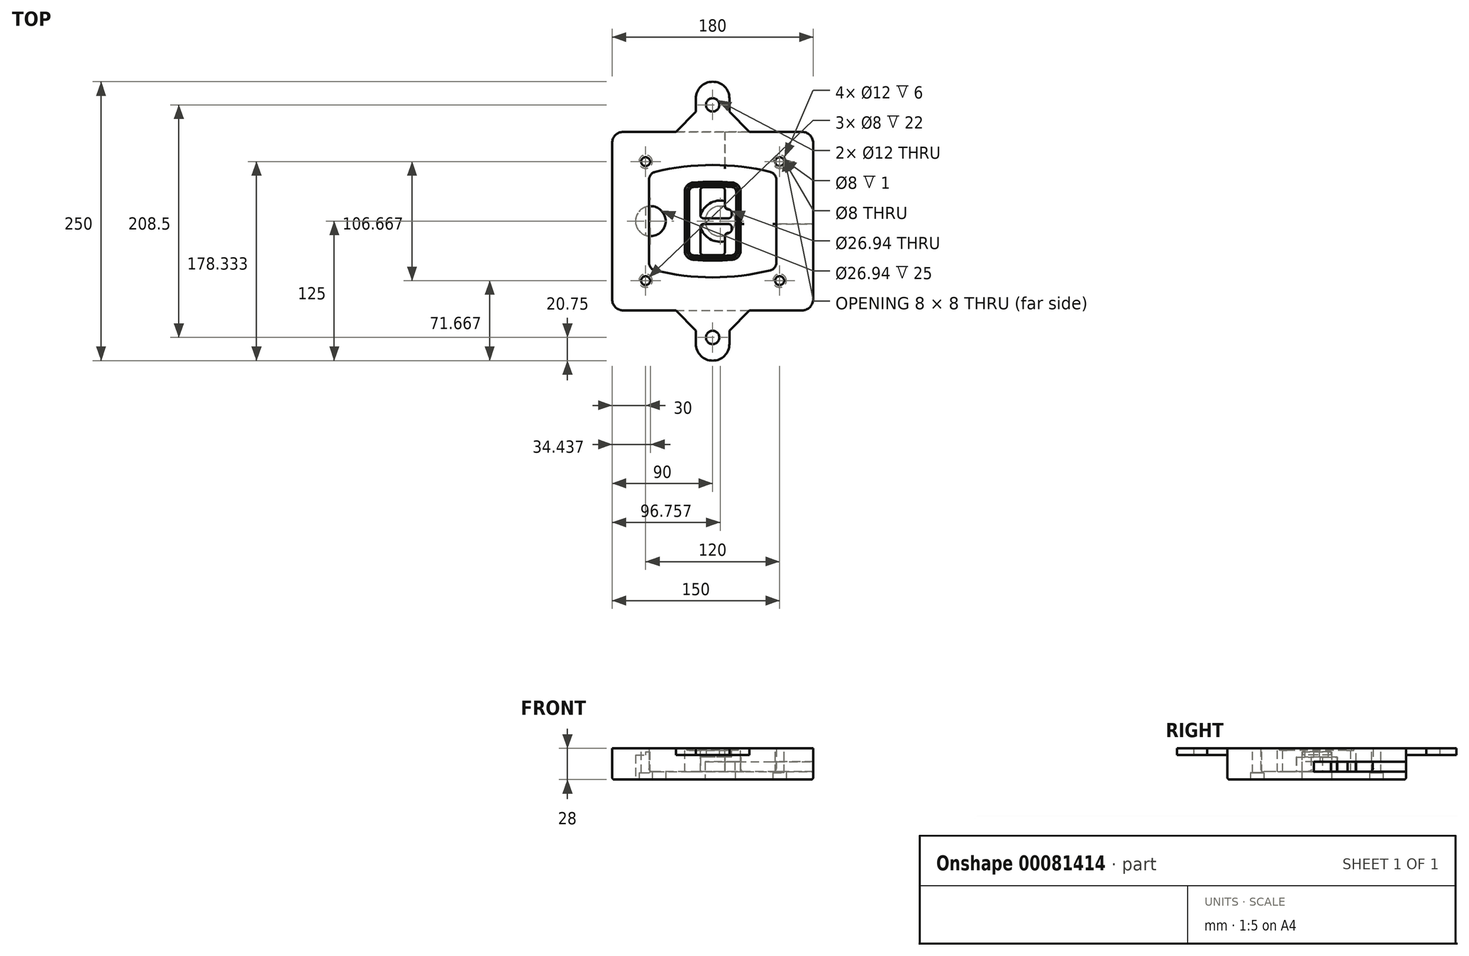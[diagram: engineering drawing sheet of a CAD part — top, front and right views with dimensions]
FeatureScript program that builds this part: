
annotation { "Feature Type Name" : "Feature", "Feature Type Description" : "" }
export const myFeature = defineFeature(function(context is Context, id is Id, definition is map)
    precondition{}
    {
        {
            var Q0;
            Q0=qCreatedBy(makeId("Top.planeOp"),FACE);
            var sketch = newSketch(context, id + "F0", { "sketchPlane" : qUnion([Q0])});
            skPoint(sketch, "E0.rect.middle", {"position": v(0, 0) * mm});
            skLineSegment(sketch, "E1.bottom", {"start": v(-80, -80) * mm, "end": v(80, -80) * mm});
            skLineSegment(sketch, "E1.top", {"start": v(-80, 80) * mm, "end": v(80, 80) * mm});
            skLineSegment(sketch, "E1.left", {"start": v(-90, -70) * mm, "end": v(-90, 70) * mm});
            skLineSegment(sketch, "E1.right", {"start": v(90, -70) * mm, "end": v(90, 70) * mm});
            skLineSegment(sketch, "E2", {"start": v(-90, 80) * mm, "end": v(90, -80) * mm, "construction": true});
            skLineSegment(sketch, "E3", {"start": v(90, 80) * mm, "end": v(-90, -80) * mm, "construction": true});
            skCircle(sketch, "E4", {"center": v(-60, 53.33) * mm, "radius": 4 * mm});
            skCircle(sketch, "E5", {"center": v(60, 53.33) * mm, "radius": 4 * mm});
            skCircle(sketch, "E6", {"center": v(60, -53.33) * mm, "radius": 4 * mm});
            skCircle(sketch, "E7", {"center": v(-60, -53.33) * mm, "radius": 4 * mm});
            skLineSegment(sketch, "E8", {"start": v(-60, 53.33) * mm, "end": v(60, 53.33) * mm, "construction": true});
            skLineSegment(sketch, "E9", {"start": v(60, 53.33) * mm, "end": v(60, -53.33) * mm, "construction": true});
            skLineSegment(sketch, "E10", {"start": v(60, -53.33) * mm, "end": v(-60, -53.33) * mm, "construction": true});
            skLineSegment(sketch, "E11", {"start": v(-60, -53.33) * mm, "end": v(-60, 53.33) * mm, "construction": true});
            skLineSegment(sketch, "E12", {"start": v(-60, 37.3) * mm, "end": v(-60, -37.3) * mm});
            skLineSegment(sketch, "E13", {"start": v(60, 37.3) * mm, "end": v(60, -37.3) * mm});
            skArc(sketch, "E14", {"start": v(52.38, 47.01) * mm, "mid": v(0, 53.33) * mm, "end": v(-52.38, 47.01) * mm});
            skArc(sketch, "E15", {"start": v(-52.38, -47.01) * mm, "mid": v(0, -53.33) * mm, "end": v(52.38, -47.01) * mm});
            skLineSegment(sketch, "E16", {"start": v(-60, 0) * mm, "end": v(60, 0) * mm, "construction": true});
            skPoint(sketch, "E17.visualSharp", {"position": v(-60, -45) * mm});
            skArc(sketch, "E17.filletArc", {"start": v(-60, -37.3) * mm, "mid": v(-57.87, -43.47) * mm, "end": v(-52.38, -47.01) * mm});
            skPoint(sketch, "E18.visualSharp", {"position": v(-60, 45) * mm});
            skArc(sketch, "E18.filletArc", {"start": v(-52.38, 47.01) * mm, "mid": v(-57.87, 43.47) * mm, "end": v(-60, 37.3) * mm});
            skPoint(sketch, "E19.visualSharp", {"position": v(60, 45) * mm});
            skArc(sketch, "E19.filletArc", {"start": v(60, 37.3) * mm, "mid": v(57.87, 43.47) * mm, "end": v(52.38, 47.01) * mm});
            skPoint(sketch, "E20.visualSharp", {"position": v(60, -45) * mm});
            skArc(sketch, "E20.filletArc", {"start": v(52.38, -47.01) * mm, "mid": v(57.87, -43.47) * mm, "end": v(60, -37.3) * mm});
            skPoint(sketch, "E21.visualSharp", {"position": v(-90, 80) * mm});
            skArc(sketch, "E21.filletArc", {"start": v(-80, 80) * mm, "mid": v(-87.07, 77.07) * mm, "end": v(-90, 70) * mm});
            skPoint(sketch, "E22.visualSharp", {"position": v(90, 80) * mm});
            skArc(sketch, "E22.filletArc", {"start": v(90, 70) * mm, "mid": v(87.07, 77.07) * mm, "end": v(80, 80) * mm});
            skPoint(sketch, "E23.visualSharp", {"position": v(90, -80) * mm});
            skArc(sketch, "E23.filletArc", {"start": v(80, -80) * mm, "mid": v(87.07, -77.07) * mm, "end": v(90, -70) * mm});
            skPoint(sketch, "E24.visualSharp", {"position": v(-90, -80) * mm});
            skArc(sketch, "E24.filletArc", {"start": v(-90, -70) * mm, "mid": v(-87.07, -77.07) * mm, "end": v(-80, -80) * mm});
            skArc(sketch, "E25.0", {"start": v(57, 37.3) * mm, "mid": v(55.5, 41.62) * mm, "end": v(51.67, 44.1) * mm});
            skLineSegment(sketch, "E25.1", {"start": v(57, 37.3) * mm, "end": v(57, -37.3) * mm});
            skArc(sketch, "E25.2", {"start": v(51.67, -44.1) * mm, "mid": v(55.5, -41.62) * mm, "end": v(57, -37.3) * mm});
            skArc(sketch, "E25.3", {"start": v(-51.67, -44.1) * mm, "mid": v(0, -50.33) * mm, "end": v(51.67, -44.1) * mm});
            skArc(sketch, "E25.4", {"start": v(-57, -37.3) * mm, "mid": v(-55.5, -41.62) * mm, "end": v(-51.67, -44.1) * mm});
            skArc(sketch, "E25.5", {"start": v(51.67, 44.1) * mm, "mid": v(0, 50.33) * mm, "end": v(-51.67, 44.1) * mm});
            skLineSegment(sketch, "E25.6", {"start": v(-57, 37.3) * mm, "end": v(-57, -37.3) * mm});
            skArc(sketch, "E25.7", {"start": v(-51.67, 44.1) * mm, "mid": v(-55.5, 41.62) * mm, "end": v(-57, 37.3) * mm});
            skArc(sketch, "E26.0", {"start": v(-53.33, 50.9) * mm, "mid": v(-61.01, 45.94) * mm, "end": v(-64, 37.3) * mm});
            skArc(sketch, "E26.1", {"start": v(53.33, 50.9) * mm, "mid": v(0, 57.33) * mm, "end": v(-53.33, 50.9) * mm});
            skArc(sketch, "E26.2", {"start": v(64, 37.3) * mm, "mid": v(61.01, 45.94) * mm, "end": v(53.33, 50.9) * mm});
            skLineSegment(sketch, "E26.3", {"start": v(64, 37.3) * mm, "end": v(64, -37.3) * mm});
            skArc(sketch, "E26.4", {"start": v(53.33, -50.9) * mm, "mid": v(61.01, -45.94) * mm, "end": v(64, -37.3) * mm});
            skLineSegment(sketch, "E26.5", {"start": v(-64, 37.3) * mm, "end": v(-64, -37.3) * mm});
            skArc(sketch, "E26.6", {"start": v(-53.33, -50.9) * mm, "mid": v(0, -57.33) * mm, "end": v(53.33, -50.9) * mm});
            skArc(sketch, "E26.7", {"start": v(-64, -37.3) * mm, "mid": v(-61.01, -45.94) * mm, "end": v(-53.33, -50.9) * mm});
            skSolve(sketch);
        }
        {
            var Q0;
            Q0=makeQuery(id+"F0.imprint","IMPRINT",FACE,{"disambiguationData":[TD([[makeQuery(id+"F0.imprint","IMPRINT",EDGE,{"derivedFrom":sQuery(id+"F0.wireOp",EDGE,"E1.bottom")}),1.0]])]});
            var Q1;
            Q1=makeQuery(id+"F0.imprint","IMPRINT",FACE,{"disambiguationData":[TD([[makeQuery(id+"F0.imprint","IMPRINT",EDGE,{"derivedFrom":sQuery(id+"F0.wireOp",EDGE,"E12")}),1.0]])]});
            var Q2;
            Q2=makeQuery(id+"F0.imprint","IMPRINT",FACE,{"disambiguationData":[TD([[makeQuery(id+"F0.imprint","IMPRINT",EDGE,{"derivedFrom":sQuery(id+"F0.wireOp",EDGE,"E25.0")}),1.0]])]});
            var Q3;
            Q3=makeQuery(id+"F0.imprint","IMPRINT",FACE,{"disambiguationData":[TD([[makeQuery(id+"F0.imprint","IMPRINT",EDGE,{"derivedFrom":sQuery(id+"F0.wireOp",EDGE,"E12")}),-1.0]])]});
            extrude(context, id + "F1", {"entities" : qUnion([Q0, Q1, Q2, Q3]), "oppositeDirection" : true, "depth" : 25 * mm});
        }
        {
            var Q0;
            Q0=makeQuery(id+"F0.imprint","IMPRINT",FACE,{"disambiguationData":[TD([[makeQuery(id+"F0.imprint","IMPRINT",EDGE,{"derivedFrom":sQuery(id+"F0.wireOp",EDGE,"E12")}),1.0]])]});
            extrude(context, id + "F2", {"entities" : qUnion([Q0]), "operationType" : NewBodyOperationType.ADD, "depth" : 3 * mm});
        }
        {
            var Q0;
            Q0=makeQuery(id+"F0.imprint","IMPRINT",FACE,{"disambiguationData":[TD([[makeQuery(id+"F0.imprint","IMPRINT",EDGE,{"derivedFrom":sQuery(id+"F0.wireOp",EDGE,"E25.0")}),1.0]])]});
            extrude(context, id + "F3", {"entities" : qUnion([Q0]), "operationType" : NewBodyOperationType.REMOVE, "oppositeDirection" : true, "depth" : 18 * mm});
        }
        {
            var Q0;
            Q0=makeQuery(id+"F2.opExtrude","CAP_FACE",FACE,{"disambiguationData":[OSD([sQuery(id+"F0.wireOp",EDGE,"E12"),sQuery(id+"F0.wireOp",EDGE,"E13"),sQuery(id+"F0.wireOp",EDGE,"E14"),sQuery(id+"F0.wireOp",EDGE,"E15"),sQuery(id+"F0.wireOp",EDGE,"E17.filletArc"),sQuery(id+"F0.wireOp",EDGE,"E18.filletArc"),sQuery(id+"F0.wireOp",EDGE,"E19.filletArc"),sQuery(id+"F0.wireOp",EDGE,"E20.filletArc"),sQuery(id+"F0.wireOp",EDGE,"E25.0"),sQuery(id+"F0.wireOp",EDGE,"E25.1"),sQuery(id+"F0.wireOp",EDGE,"E25.2"),sQuery(id+"F0.wireOp",EDGE,"E25.3"),sQuery(id+"F0.wireOp",EDGE,"E25.4"),sQuery(id+"F0.wireOp",EDGE,"E25.5"),sQuery(id+"F0.wireOp",EDGE,"E25.6"),sQuery(id+"F0.wireOp",EDGE,"E25.7")])],"isStart":false});
            var sketch = newSketch(context, id + "F4", { "sketchPlane" : qUnion([Q0])});
            skArc(sketch, "E27.0", {"start": v(-17.7, -34.56) * mm, "mid": v(0, -35.33) * mm, "end": v(17.7, -34.56) * mm});
            skArc(sketch, "E28.0", {"start": v(17.7, 34.56) * mm, "mid": v(0, 35.33) * mm, "end": v(-17.7, 34.56) * mm});
            skLineSegment(sketch, "E29", {"start": v(-25, 26.59) * mm, "end": v(-25, -26.59) * mm});
            skLineSegment(sketch, "E30", {"start": v(25, 26.59) * mm, "end": v(25, -26.59) * mm});
            skLineSegment(sketch, "E31", {"start": v(-25, 33.78) * mm, "end": v(25, 33.78) * mm, "construction": true});
            skLineSegment(sketch, "E32", {"start": v(-25, -33.78) * mm, "end": v(25, -33.78) * mm, "construction": true});
            skPoint(sketch, "E33.visualSharp", {"position": v(-25, 33.78) * mm});
            skArc(sketch, "E33.filletArc", {"start": v(-17.7, 34.56) * mm, "mid": v(-22.9, 32) * mm, "end": v(-25, 26.59) * mm});
            skPoint(sketch, "E34.visualSharp", {"position": v(25, 33.78) * mm});
            skArc(sketch, "E34.filletArc", {"start": v(25, 26.59) * mm, "mid": v(22.9, 32) * mm, "end": v(17.7, 34.56) * mm});
            skPoint(sketch, "E35.visualSharp", {"position": v(25, -33.78) * mm});
            skArc(sketch, "E35.filletArc", {"start": v(17.7, -34.56) * mm, "mid": v(22.9, -32) * mm, "end": v(25, -26.59) * mm});
            skPoint(sketch, "E36.visualSharp", {"position": v(-25, -33.78) * mm});
            skArc(sketch, "E36.filletArc", {"start": v(-25, -26.59) * mm, "mid": v(-22.9, -32) * mm, "end": v(-17.7, -34.56) * mm});
            skArc(sketch, "E37.0", {"start": v(51.67, 44.1) * mm, "mid": v(0, 50.33) * mm, "end": v(-51.67, 44.1) * mm});
            skArc(sketch, "E37.1", {"start": v(-51.67, 44.1) * mm, "mid": v(-55.5, 41.62) * mm, "end": v(-57, 37.3) * mm});
            skLineSegment(sketch, "E37.2", {"start": v(-57, 37.3) * mm, "end": v(-57, -37.3) * mm});
            skArc(sketch, "E37.3", {"start": v(-57, -37.3) * mm, "mid": v(-55.5, -41.62) * mm, "end": v(-51.67, -44.1) * mm});
            skArc(sketch, "E37.4", {"start": v(-51.67, -44.1) * mm, "mid": v(0, -50.33) * mm, "end": v(51.67, -44.1) * mm});
            skArc(sketch, "E37.5", {"start": v(51.67, -44.1) * mm, "mid": v(55.5, -41.62) * mm, "end": v(57, -37.3) * mm});
            skLineSegment(sketch, "E37.6", {"start": v(57, 37.3) * mm, "end": v(57, -37.3) * mm});
            skArc(sketch, "E37.7", {"start": v(57, 37.3) * mm, "mid": v(55.5, 41.62) * mm, "end": v(51.67, 44.1) * mm});
            skLineSegment(sketch, "E38.0", {"start": v(23, 26.59) * mm, "end": v(23, -26.59) * mm});
            skArc(sketch, "E38.1", {"start": v(17.53, -32.56) * mm, "mid": v(21.42, -30.64) * mm, "end": v(23, -26.59) * mm});
            skArc(sketch, "E38.2", {"start": v(-17.53, -32.56) * mm, "mid": v(0, -33.33) * mm, "end": v(17.53, -32.56) * mm});
            skArc(sketch, "E38.3", {"start": v(-23, -26.59) * mm, "mid": v(-21.42, -30.64) * mm, "end": v(-17.53, -32.56) * mm});
            skLineSegment(sketch, "E38.4", {"start": v(-23, 26.59) * mm, "end": v(-23, -26.59) * mm});
            skArc(sketch, "E38.5", {"start": v(23, 26.59) * mm, "mid": v(21.42, 30.64) * mm, "end": v(17.53, 32.56) * mm});
            skArc(sketch, "E38.6", {"start": v(-17.53, 32.56) * mm, "mid": v(-21.42, 30.64) * mm, "end": v(-23, 26.59) * mm});
            skArc(sketch, "E38.7", {"start": v(17.53, 32.56) * mm, "mid": v(0, 33.33) * mm, "end": v(-17.53, 32.56) * mm});
            skArc(sketch, "E39.0", {"start": v(21, 26.59) * mm, "mid": v(19.95, 29.29) * mm, "end": v(17.35, 30.57) * mm});
            skLineSegment(sketch, "E39.1", {"start": v(21, 26.59) * mm, "end": v(21, -26.59) * mm});
            skArc(sketch, "E39.2", {"start": v(17.35, -30.57) * mm, "mid": v(19.95, -29.29) * mm, "end": v(21, -26.59) * mm});
            skArc(sketch, "E39.3", {"start": v(-17.35, -30.57) * mm, "mid": v(0, -31.33) * mm, "end": v(17.35, -30.57) * mm});
            skArc(sketch, "E39.4", {"start": v(-21, -26.59) * mm, "mid": v(-19.95, -29.29) * mm, "end": v(-17.35, -30.57) * mm});
            skArc(sketch, "E39.5", {"start": v(17.35, 30.57) * mm, "mid": v(0, 31.33) * mm, "end": v(-17.35, 30.57) * mm});
            skLineSegment(sketch, "E39.6", {"start": v(-21, 26.59) * mm, "end": v(-21, -26.59) * mm});
            skArc(sketch, "E39.7", {"start": v(-17.35, 30.57) * mm, "mid": v(-19.95, 29.29) * mm, "end": v(-21, 26.59) * mm});
            skLineSegment(sketch, "E40", {"start": v(-25, 0) * mm, "end": v(25, 0) * mm, "construction": true});
            skLineSegment(sketch, "E41", {"start": v(-11, 5.5) * mm, "end": v(-11, 27.5) * mm});
            skLineSegment(sketch, "E42", {"start": v(-8, 30.5) * mm, "end": v(8, 30.5) * mm});
            skLineSegment(sketch, "E43", {"start": v(11, 27.5) * mm, "end": v(11, 13.5) * mm});
            skLineSegment(sketch, "E44", {"start": v(14, 10.5) * mm, "end": v(14, 10.5) * mm});
            skLineSegment(sketch, "E45", {"start": v(17, 7.5) * mm, "end": v(17, 5.5) * mm});
            skLineSegment(sketch, "E46", {"start": v(14, 2.5) * mm, "end": v(-8, 2.5) * mm});
            skPoint(sketch, "E47.visualSharp", {"position": v(-11, 30.5) * mm});
            skArc(sketch, "E47.filletArc", {"start": v(-8, 30.5) * mm, "mid": v(-10.12, 29.62) * mm, "end": v(-11, 27.5) * mm});
            skPoint(sketch, "E48.visualSharp", {"position": v(11, 30.5) * mm});
            skArc(sketch, "E48.filletArc", {"start": v(11, 27.5) * mm, "mid": v(10.12, 29.62) * mm, "end": v(8, 30.5) * mm});
            skPoint(sketch, "E49.visualSharp", {"position": v(11, 10.5) * mm});
            skArc(sketch, "E49.filletArc", {"start": v(11, 13.5) * mm, "mid": v(11.88, 11.38) * mm, "end": v(14, 10.5) * mm});
            skPoint(sketch, "E50.visualSharp", {"position": v(17, 10.5) * mm});
            skArc(sketch, "E50.filletArc", {"start": v(17, 7.5) * mm, "mid": v(16.12, 9.62) * mm, "end": v(14, 10.5) * mm});
            skPoint(sketch, "E51.visualSharp", {"position": v(17, 2.5) * mm});
            skArc(sketch, "E51.filletArc", {"start": v(14, 2.5) * mm, "mid": v(16.12, 3.38) * mm, "end": v(17, 5.5) * mm});
            skPoint(sketch, "E52.visualSharp", {"position": v(-11, 2.5) * mm});
            skArc(sketch, "E52.filletArc", {"start": v(-11, 5.5) * mm, "mid": v(-10.12, 3.38) * mm, "end": v(-8, 2.5) * mm});
            skLineSegment(sketch, "E53.0.MirrorCS", {"start": v(14, -2.5) * mm, "end": v(-8, -2.5) * mm});
            skArc(sketch, "E54.0.MirrorCS", {"start": v(-11, -5.5) * mm, "mid": v(-10.12, -3.38) * mm, "end": v(-8, -2.5) * mm});
            skLineSegment(sketch, "E55.0.MirrorCS", {"start": v(-11, -5.5) * mm, "end": v(-11, -27.5) * mm});
            skArc(sketch, "E56.0.MirrorCS", {"start": v(-8, -30.5) * mm, "mid": v(-10.12, -29.62) * mm, "end": v(-11, -27.5) * mm});
            skLineSegment(sketch, "E57.0.MirrorCS", {"start": v(-8, -30.5) * mm, "end": v(8, -30.5) * mm});
            skArc(sketch, "E58.0.MirrorCS", {"start": v(11, -27.5) * mm, "mid": v(10.12, -29.62) * mm, "end": v(8, -30.5) * mm});
            skLineSegment(sketch, "E59.0.MirrorCS", {"start": v(11, -27.5) * mm, "end": v(11, -13.5) * mm});
            skArc(sketch, "E60.0.MirrorCS", {"start": v(11, -13.5) * mm, "mid": v(11.88, -11.38) * mm, "end": v(14, -10.5) * mm});
            skArc(sketch, "E61.0.MirrorCS", {"start": v(17, -7.5) * mm, "mid": v(16.12, -9.62) * mm, "end": v(14, -10.5) * mm});
            skLineSegment(sketch, "E62.0.MirrorCS", {"start": v(17, -7.5) * mm, "end": v(17, -5.5) * mm});
            skArc(sketch, "E63.0.MirrorCS", {"start": v(14, -2.5) * mm, "mid": v(16.12, -3.38) * mm, "end": v(17, -5.5) * mm});
            skSolve(sketch);
        }
        {
            var Q0;
            Q0=makeQuery(id+"F4.imprint","IMPRINT",FACE,{"disambiguationData":[TD([[makeQuery(id+"F4.imprint","IMPRINT",EDGE,{"derivedFrom":sQuery(id+"F4.wireOp",EDGE,"E27.0")}),1.0]])]});
            var Q1;
            Q1=makeQuery(id+"F4.imprint","IMPRINT",FACE,{"disambiguationData":[TD([[makeQuery(id+"F4.imprint","IMPRINT",EDGE,{"derivedFrom":sQuery(id+"F4.wireOp",EDGE,"E38.0")}),-1.0]])]});
            var Q2;
            Q2=makeQuery(id+"F4.imprint","IMPRINT",FACE,{"disambiguationData":[TD([[makeQuery(id+"F4.imprint","IMPRINT",EDGE,{"derivedFrom":sQuery(id+"F4.wireOp",EDGE,"E39.0")}),1.0]])]});
            extrude(context, id + "F5", {"entities" : qUnion([Q0, Q1, Q2]), "operationType" : NewBodyOperationType.ADD, "endBound" : BoundingType.UP_TO_NEXT, "oppositeDirection" : true, "depth" : 25 * mm});
        }
        {
            var Q0;
            Q0=makeQuery(id+"F4.imprint","IMPRINT",FACE,{"disambiguationData":[TD([[makeQuery(id+"F4.imprint","IMPRINT",EDGE,{"derivedFrom":sQuery(id+"F4.wireOp",EDGE,"E38.0")}),-1.0]])]});
            extrude(context, id + "F6", {"entities" : qUnion([Q0]), "operationType" : NewBodyOperationType.REMOVE, "oppositeDirection" : true, "depth" : 2 * mm});
        }
        {
            var Q0;
            Q0=makeQuery(id+"F1.opExtrude","CAP_FACE",FACE,{"disambiguationData":[OSD([sQuery(id+"F0.wireOp",EDGE,"E1.bottom"),sQuery(id+"F0.wireOp",EDGE,"E1.top"),sQuery(id+"F0.wireOp",EDGE,"E1.left"),sQuery(id+"F0.wireOp",EDGE,"E1.right"),sQuery(id+"F0.wireOp",EDGE,"E4"),sQuery(id+"F0.wireOp",EDGE,"E5"),sQuery(id+"F0.wireOp",EDGE,"E6"),sQuery(id+"F0.wireOp",EDGE,"E7"),sQuery(id+"F0.wireOp",EDGE,"E21.filletArc"),sQuery(id+"F0.wireOp",EDGE,"E22.filletArc"),sQuery(id+"F0.wireOp",EDGE,"E23.filletArc"),sQuery(id+"F0.wireOp",EDGE,"E24.filletArc")])],"isStart":false});
            var sketch = newSketch(context, id + "F7", { "sketchPlane" : qUnion([Q0])});
            skCircle(sketch, "E64", {"center": v(6.76, 0) * mm, "radius": 13.47 * mm});
            skCircle(sketch, "E65", {"center": v(-55.56, 0) * mm, "radius": 13.47 * mm});
            skLineSegment(sketch, "E66", {"start": v(90, 0) * mm, "end": v(-90, 0) * mm});
            skCircle(sketch, "E67", {"center": v(6.76, 0) * mm, "radius": 18.47 * mm});
            skCircle(sketch, "E68", {"center": v(60, -53.33) * mm, "radius": 6 * mm});
            skCircle(sketch, "E69", {"center": v(-60, -53.33) * mm, "radius": 6 * mm});
            skCircle(sketch, "E70", {"center": v(-60, 53.33) * mm, "radius": 6 * mm});
            skCircle(sketch, "E71", {"center": v(60, 53.33) * mm, "radius": 6 * mm});
            skSolve(sketch);
        }
        {
            var Q0;
            {var subQ1=sQuery(id+"F7.wireOp",EDGE,"E66");var subQ4=sQuery(id+"F7.wireOp",EDGE,"E64");var subQ6=makeQuery(id+"F7.imprint","INTERSECT",VERTEX,{"disambiguationData":[OD(0.0)],"derivedFrom":[subQ4,subQ1]});Q0=makeQuery(id+"F7.imprint","IMPRINT",FACE,{"disambiguationData":[TD([[makeQuery(id+"F7.imprint","IMPRINT",EDGE,{"disambiguationData":[TD([[subQ6,-1.0]])],"derivedFrom":subQ4}),-1.0]])]});}
            var Q1;
            {var subQ0=sQuery(id+"F7.wireOp",EDGE,"E66");var subQ1=sQuery(id+"F7.wireOp",EDGE,"E64");var subQ3=makeQuery(id+"F7.imprint","INTERSECT",VERTEX,{"disambiguationData":[OD(0.0)],"derivedFrom":[subQ1,subQ0]});Q1=makeQuery(id+"F7.imprint","IMPRINT",FACE,{"disambiguationData":[TD([[makeQuery(id+"F7.imprint","IMPRINT",EDGE,{"disambiguationData":[TD([[subQ3,-1.0]])],"derivedFrom":subQ1}),1.0]])]});}
            var Q2;
            {var subQ0=sQuery(id+"F7.wireOp",EDGE,"E66");var subQ1=sQuery(id+"F7.wireOp",EDGE,"E64");var subQ3=makeQuery(id+"F7.imprint","INTERSECT",VERTEX,{"disambiguationData":[OD(0.0)],"derivedFrom":[subQ1,subQ0]});Q2=makeQuery(id+"F7.imprint","IMPRINT",FACE,{"disambiguationData":[TD([[makeQuery(id+"F7.imprint","IMPRINT",EDGE,{"disambiguationData":[TD([[subQ3,1.0]])],"derivedFrom":subQ1}),1.0]])]});}
            var Q3;
            {var subQ1=sQuery(id+"F7.wireOp",EDGE,"E66");var subQ4=sQuery(id+"F7.wireOp",EDGE,"E64");var subQ6=makeQuery(id+"F7.imprint","INTERSECT",VERTEX,{"disambiguationData":[OD(0.0)],"derivedFrom":[subQ4,subQ1]});Q3=makeQuery(id+"F7.imprint","IMPRINT",FACE,{"disambiguationData":[TD([[makeQuery(id+"F7.imprint","IMPRINT",EDGE,{"disambiguationData":[TD([[subQ6,1.0]])],"derivedFrom":subQ4}),-1.0]])]});}
            extrude(context, id + "F8", {"entities" : qUnion([Q0, Q1, Q2, Q3]), "operationType" : NewBodyOperationType.ADD, "oppositeDirection" : true, "depth" : 20 * mm});
        }
        {
            var Q0;
            {var subQ0=sQuery(id+"F7.wireOp",EDGE,"E66");var subQ1=sQuery(id+"F7.wireOp",EDGE,"E64");var subQ3=makeQuery(id+"F7.imprint","INTERSECT",VERTEX,{"disambiguationData":[OD(0.0)],"derivedFrom":[subQ1,subQ0]});Q0=makeQuery(id+"F7.imprint","IMPRINT",FACE,{"disambiguationData":[TD([[makeQuery(id+"F7.imprint","IMPRINT",EDGE,{"disambiguationData":[TD([[subQ3,-1.0]])],"derivedFrom":subQ1}),1.0]])]});}
            var Q1;
            {var subQ0=sQuery(id+"F7.wireOp",EDGE,"E66");var subQ1=sQuery(id+"F7.wireOp",EDGE,"E64");var subQ3=makeQuery(id+"F7.imprint","INTERSECT",VERTEX,{"disambiguationData":[OD(0.0)],"derivedFrom":[subQ1,subQ0]});Q1=makeQuery(id+"F7.imprint","IMPRINT",FACE,{"disambiguationData":[TD([[makeQuery(id+"F7.imprint","IMPRINT",EDGE,{"disambiguationData":[TD([[subQ3,1.0]])],"derivedFrom":subQ1}),1.0]])]});}
            extrude(context, id + "F9", {"entities" : qUnion([Q0, Q1]), "operationType" : NewBodyOperationType.REMOVE, "oppositeDirection" : true, "depth" : 16 * mm});
        }
        {
            var Q0;
            {var subQ0=sQuery(id+"F7.wireOp",EDGE,"E66");var subQ1=sQuery(id+"F7.wireOp",EDGE,"E65");var subQ3=makeQuery(id+"F7.imprint","INTERSECT",VERTEX,{"disambiguationData":[OD(0.0)],"derivedFrom":[subQ1,subQ0]});Q0=makeQuery(id+"F7.imprint","IMPRINT",FACE,{"disambiguationData":[TD([[makeQuery(id+"F7.imprint","IMPRINT",EDGE,{"disambiguationData":[TD([[subQ3,-1.0]])],"derivedFrom":subQ1}),1.0]])]});}
            var Q1;
            {var subQ0=sQuery(id+"F7.wireOp",EDGE,"E66");var subQ1=sQuery(id+"F7.wireOp",EDGE,"E65");var subQ3=makeQuery(id+"F7.imprint","INTERSECT",VERTEX,{"disambiguationData":[OD(0.0)],"derivedFrom":[subQ1,subQ0]});Q1=makeQuery(id+"F7.imprint","IMPRINT",FACE,{"disambiguationData":[TD([[makeQuery(id+"F7.imprint","IMPRINT",EDGE,{"disambiguationData":[TD([[subQ3,1.0]])],"derivedFrom":subQ1}),1.0]])]});}
            extrude(context, id + "F10", {"entities" : qUnion([Q0, Q1]), "operationType" : NewBodyOperationType.REMOVE, "oppositeDirection" : true, "depth" : 25 * mm});
        }
        {
            var Q0;
            Q0=makeQuery(id+"F7.imprint","IMPRINT",FACE,{"disambiguationData":[TD([[makeQuery(id+"F7.imprint","IMPRINT",EDGE,{"derivedFrom":sQuery(id+"F7.wireOp",EDGE,"E68")}),1.0]])]});
            var Q1;
            Q1=makeQuery(id+"F7.imprint","IMPRINT",FACE,{"disambiguationData":[TD([[makeQuery(id+"F7.imprint","IMPRINT",EDGE,{"derivedFrom":makeQuery(id+"F1.opExtrude","CAP_EDGE",EDGE,{"disambiguationData":[OSD([sQuery(id+"F0.wireOp",EDGE,"E5")])],"isStart":false})}),-1.0]])]});
            var Q2;
            Q2=makeQuery(id+"F7.imprint","IMPRINT",FACE,{"disambiguationData":[TD([[makeQuery(id+"F7.imprint","IMPRINT",EDGE,{"derivedFrom":sQuery(id+"F7.wireOp",EDGE,"E69")}),1.0]])]});
            var Q3;
            Q3=makeQuery(id+"F7.imprint","IMPRINT",FACE,{"disambiguationData":[TD([[makeQuery(id+"F7.imprint","IMPRINT",EDGE,{"derivedFrom":makeQuery(id+"F1.opExtrude","CAP_EDGE",EDGE,{"disambiguationData":[OSD([sQuery(id+"F0.wireOp",EDGE,"E4")])],"isStart":false})}),-1.0]])]});
            var Q4;
            Q4=makeQuery(id+"F7.imprint","IMPRINT",FACE,{"disambiguationData":[TD([[makeQuery(id+"F7.imprint","IMPRINT",EDGE,{"derivedFrom":sQuery(id+"F7.wireOp",EDGE,"E70")}),1.0]])]});
            var Q5;
            Q5=makeQuery(id+"F7.imprint","IMPRINT",FACE,{"disambiguationData":[TD([[makeQuery(id+"F7.imprint","IMPRINT",EDGE,{"derivedFrom":makeQuery(id+"F1.opExtrude","CAP_EDGE",EDGE,{"disambiguationData":[OSD([sQuery(id+"F0.wireOp",EDGE,"E7")])],"isStart":false})}),-1.0]])]});
            var Q6;
            Q6=makeQuery(id+"F7.imprint","IMPRINT",FACE,{"disambiguationData":[TD([[makeQuery(id+"F7.imprint","IMPRINT",EDGE,{"derivedFrom":sQuery(id+"F7.wireOp",EDGE,"E71")}),1.0]])]});
            var Q7;
            Q7=makeQuery(id+"F7.imprint","IMPRINT",FACE,{"disambiguationData":[TD([[makeQuery(id+"F7.imprint","IMPRINT",EDGE,{"derivedFrom":makeQuery(id+"F1.opExtrude","CAP_EDGE",EDGE,{"disambiguationData":[OSD([sQuery(id+"F0.wireOp",EDGE,"E6")])],"isStart":false})}),-1.0]])]});
            extrude(context, id + "F11", {"entities" : qUnion([Q0, Q1, Q2, Q3, Q4, Q5, Q6, Q7]), "operationType" : NewBodyOperationType.REMOVE, "oppositeDirection" : true, "depth" : 6 * mm});
        }
        {
            var Q0;
            Q0=makeQuery(id+"F9.boolean.opBoolean","COPY",FACE,{"derivedFrom":makeQuery(id+"F9.opExtrude","CAP_FACE",FACE,{"disambiguationData":[OSD([sQuery(id+"F7.wireOp",EDGE,"E64")])],"isStart":false})});
            var sketch = newSketch(context, id + "F12", { "sketchPlane" : qUnion([Q0])});
            skArc(sketch, "E72.0", {"start": v(11, -88.19) * mm, "mid": v(97.1, -83.6) * mm, "end": v(92.5, 2.5) * mm});
            skLineSegment(sketch, "E72.1", {"start": v(11, -17.97) * mm, "end": v(11, -17.97) * mm});
            skLineSegment(sketch, "E73", {"start": v(92.5, -105.13) * mm, "end": v(102.3, -105.13) * mm});
            skLineSegment(sketch, "E74.0", {"start": v(92.5, 2.5) * mm, "end": v(14, 2.5) * mm});
            skArc(sketch, "E74.1", {"start": v(14, 2.5) * mm, "mid": v(16.12, 3.38) * mm, "end": v(17, 5.5) * mm});
            skLineSegment(sketch, "E74.2", {"start": v(17, 7.5) * mm, "end": v(17, 5.5) * mm});
            skArc(sketch, "E74.3", {"start": v(17, 7.5) * mm, "mid": v(16.12, 9.62) * mm, "end": v(14, 10.5) * mm});
            skArc(sketch, "E74.4", {"start": v(11, 13.5) * mm, "mid": v(11.88, 11.38) * mm, "end": v(14, 10.5) * mm});
            skLineSegment(sketch, "E74.5", {"start": v(11, 13.5) * mm, "end": v(11, -88.19) * mm});
            skLineSegment(sketch, "E74.7", {"start": v(92.5, -2.5) * mm, "end": v(14, -2.5) * mm});
            skArc(sketch, "E74.8", {"start": v(14, -2.5) * mm, "mid": v(16.12, -3.38) * mm, "end": v(17, -5.5) * mm});
            skLineSegment(sketch, "E74.9", {"start": v(17, -7.5) * mm, "end": v(17, -5.5) * mm});
            skArc(sketch, "E74.10", {"start": v(17, -7.5) * mm, "mid": v(16.12, -9.62) * mm, "end": v(14, -10.5) * mm});
            skArc(sketch, "E74.11", {"start": v(11, -13.5) * mm, "mid": v(11.88, -11.38) * mm, "end": v(14, -10.5) * mm});
            skLineSegment(sketch, "E74.12", {"start": v(11, -17.97) * mm, "end": v(11, -13.5) * mm});
            skPoint(sketch, "E75.orphan", {"position": v(11, -27.5) * mm});
            skPoint(sketch, "E76.orphan", {"position": v(-8, -2.5) * mm});
            skPoint(sketch, "E77.orphan", {"position": v(-8, 2.5) * mm});
            skPoint(sketch, "E78.orphan", {"position": v(11, 27.5) * mm});
            skSolve(sketch);
        }
        {
            var Q0;
            {var subQ7=sQuery(id+"F12.wireOp",EDGE,"E72.0");var subQ14=sQuery(id+"F12.wireOp",EDGE,"E72.1");var subQ16=sQuery(id+"F12.wireOp",EDGE,"E74.1");var subQ18=sQuery(id+"F12.wireOp",EDGE,"E74.8");Q0=qUnion([makeQuery(id+"F12.imprint","IMPRINT",FACE,{"disambiguationData":[TD([[makeQuery(id+"F12.imprint","IMPRINT",EDGE,{"derivedFrom":subQ7}),1.0]])]}),makeQuery(id+"F12.imprint","IMPRINT",FACE,{"disambiguationData":[TD([[makeQuery(id+"F12.imprint","IMPRINT",EDGE,{"derivedFrom":subQ14}),1.0]])]}),makeQuery(id+"F12.imprint","IMPRINT",FACE,{"disambiguationData":[TD([[makeQuery(id+"F12.imprint","IMPRINT",EDGE,{"derivedFrom":subQ16}),1.0]])]}),makeQuery(id+"F12.imprint","IMPRINT",FACE,{"disambiguationData":[TD([[makeQuery(id+"F12.imprint","IMPRINT",EDGE,{"derivedFrom":subQ18}),-1.0]])]})]);}
            var Q1;
            Q1=makeQuery(id+"F5.boolean.opBoolean","SPLIT",FACE,{"disambiguationData":[TD([makeQuery(id+"F5.opExtrude","SWEPT_FACE",FACE,{"disambiguationData":[OSD([sQuery(id+"F4.wireOp",EDGE,"E41")])]})])],"derivedFrom":makeQuery(id+"F3.boolean.opBoolean","COPY",FACE,{"derivedFrom":makeQuery(id+"F3.opExtrude","CAP_FACE",FACE,{"disambiguationData":[OSD([sQuery(id+"F0.wireOp",EDGE,"E25.0"),sQuery(id+"F0.wireOp",EDGE,"E25.1"),sQuery(id+"F0.wireOp",EDGE,"E25.2"),sQuery(id+"F0.wireOp",EDGE,"E25.3"),sQuery(id+"F0.wireOp",EDGE,"E25.4"),sQuery(id+"F0.wireOp",EDGE,"E25.5"),sQuery(id+"F0.wireOp",EDGE,"E25.6"),sQuery(id+"F0.wireOp",EDGE,"E25.7")])],"isStart":false})})});
            extrude(context, id + "F13", {"entities" : qUnion([Q0]), "operationType" : NewBodyOperationType.REMOVE, "endBound" : BoundingType.UP_TO_SURFACE, "endBoundEntityFace" : qUnion([Q1]), "depth" : 25 * mm});
        }
        {
            var Q0;
            Q0=makeQuery(id+"F3.boolean.opBoolean","COPY",EDGE,{"derivedFrom":makeQuery(id+"F3.opExtrude","CAP_EDGE",EDGE,{"disambiguationData":[OSD([sQuery(id+"F0.wireOp",EDGE,"E25.6")])],"isStart":false})});
            var Q1;
            Q1=makeQuery(id+"F8.boolean.opBoolean","INTERSECT",EDGE,{"derivedFrom":[makeQuery(id+"F5.opExtrude","SWEPT_FACE",FACE,{"disambiguationData":[OSD([sQuery(id+"F4.wireOp",EDGE,"E30")])]}),makeQuery(id+"F8.opExtrude","CAP_FACE",FACE,{"disambiguationData":[OSD([sQuery(id+"F7.wireOp",EDGE,"E67")])],"isStart":false})]});
            var Q2;
            Q2=makeQuery(id+"F8.boolean.opBoolean","INTERSECT",EDGE,{"disambiguationData":[OD(1.0)],"derivedFrom":[makeQuery(id+"F5.opExtrude","SWEPT_FACE",FACE,{"disambiguationData":[OSD([sQuery(id+"F4.wireOp",EDGE,"E30")])]}),makeQuery(id+"F8.opExtrude","SWEPT_FACE",FACE,{"disambiguationData":[OSD([sQuery(id+"F7.wireOp",EDGE,"E67")])]})]});
            var Q3;
            {var subQ0=makeQuery(id+"F3.boolean.opBoolean","COPY",FACE,{"derivedFrom":makeQuery(id+"F3.opExtrude","CAP_FACE",FACE,{"disambiguationData":[OSD([sQuery(id+"F0.wireOp",EDGE,"E25.0"),sQuery(id+"F0.wireOp",EDGE,"E25.1"),sQuery(id+"F0.wireOp",EDGE,"E25.2"),sQuery(id+"F0.wireOp",EDGE,"E25.3"),sQuery(id+"F0.wireOp",EDGE,"E25.4"),sQuery(id+"F0.wireOp",EDGE,"E25.5"),sQuery(id+"F0.wireOp",EDGE,"E25.6"),sQuery(id+"F0.wireOp",EDGE,"E25.7")])],"isStart":false})});var subQ1=sQuery(id+"F4.wireOp",EDGE,"E30");Q3=makeQuery(id+"F8.boolean.opBoolean","SPLIT",EDGE,{"disambiguationData":[TD([makeQuery(id+"F5.opExtrude","SWEPT_FACE",FACE,{"disambiguationData":[OSD([sQuery(id+"F4.wireOp",EDGE,"E35.filletArc")])]})])],"derivedFrom":makeQuery(id+"F5.opExtrude","TWEAK_EDGE",EDGE,{"derivedFrom":[subQ0,makeQuery(id+"F4.imprint","IMPRINT",EDGE,{"derivedFrom":subQ1})]})});}
            var Q4;
            {var subQ0=sQuery(id+"F0.wireOp",EDGE,"E25.0");var subQ1=sQuery(id+"F0.wireOp",EDGE,"E25.1");var subQ2=sQuery(id+"F0.wireOp",EDGE,"E25.2");var subQ3=sQuery(id+"F0.wireOp",EDGE,"E25.3");var subQ4=sQuery(id+"F0.wireOp",EDGE,"E25.4");var subQ5=sQuery(id+"F0.wireOp",EDGE,"E25.5");var subQ6=sQuery(id+"F0.wireOp",EDGE,"E25.6");var subQ7=sQuery(id+"F0.wireOp",EDGE,"E25.7");Q4=makeQuery(id+"F8.boolean.opBoolean","INTERSECT",EDGE,{"derivedFrom":[makeQuery(id+"F5.boolean.opBoolean","SPLIT",FACE,{"disambiguationData":[TD([makeQuery(id+"F2.opExtrude","SWEPT_FACE",FACE,{"disambiguationData":[OSD([subQ0])]})])],"derivedFrom":makeQuery(id+"F3.boolean.opBoolean","COPY",FACE,{"derivedFrom":makeQuery(id+"F3.opExtrude","CAP_FACE",FACE,{"disambiguationData":[OSD([subQ0,subQ1,subQ2,subQ3,subQ4,subQ5,subQ6,subQ7])],"isStart":false})})}),makeQuery(id+"F8.opExtrude","SWEPT_FACE",FACE,{"disambiguationData":[OSD([sQuery(id+"F7.wireOp",EDGE,"E67")])]})]});}
            var Q5;
            Q5=makeQuery(id+"F8.boolean.opBoolean","INTERSECT",EDGE,{"disambiguationData":[OD(0.0)],"derivedFrom":[makeQuery(id+"F5.opExtrude","SWEPT_FACE",FACE,{"disambiguationData":[OSD([sQuery(id+"F4.wireOp",EDGE,"E30")])]}),makeQuery(id+"F8.opExtrude","SWEPT_FACE",FACE,{"disambiguationData":[OSD([sQuery(id+"F7.wireOp",EDGE,"E67")])]})]});
            fillet(context, id + "F14", {"entities" : qUnion([Q0, Q1, Q2, Q3, Q4, Q5]), "radius" : 3 * mm, "tangentPropagation" : true, "allowEdgeOverflow" : false});
        }
        {
            var Q0;
            Q0=makeQuery(id+"F1.opExtrude","CAP_EDGE",EDGE,{"disambiguationData":[OSD([sQuery(id+"F0.wireOp",EDGE,"E1.bottom")])],"isStart":false});
            fillet(context, id + "F15", {"entities" : qUnion([Q0]), "radius" : 2 * mm, "tangentPropagation" : true, "allowEdgeOverflow" : false});
        }
        {
            var Q0;
            {var subQ0=sQuery(id+"F0.wireOp",EDGE,"E22.filletArc");var subQ1=sQuery(id+"F0.wireOp",EDGE,"E7");var subQ2=sQuery(id+"F0.wireOp",EDGE,"E6");var subQ3=sQuery(id+"F0.wireOp",EDGE,"E5");var subQ4=sQuery(id+"F0.wireOp",EDGE,"E4");var subQ5=sQuery(id+"F0.wireOp",EDGE,"E1.bottom");var subQ6=sQuery(id+"F0.wireOp",EDGE,"E21.filletArc");var subQ7=sQuery(id+"F0.wireOp",EDGE,"E1.top");var subQ8=sQuery(id+"F0.wireOp",EDGE,"E1.left");var subQ9=sQuery(id+"F0.wireOp",EDGE,"E1.right");var subQ10=sQuery(id+"F0.wireOp",EDGE,"E23.filletArc");var subQ11=sQuery(id+"F0.wireOp",EDGE,"E24.filletArc");Q0=makeQuery(id+"F2.boolean.opBoolean","SPLIT",FACE,{"disambiguationData":[TD([makeQuery(id+"F1.opExtrude","SWEPT_FACE",FACE,{"disambiguationData":[OSD([subQ5])]})])],"derivedFrom":makeQuery(id+"F1.opExtrude","CAP_FACE",FACE,{"disambiguationData":[OSD([subQ5,subQ7,subQ8,subQ9,subQ4,subQ3,subQ2,subQ1,subQ6,subQ0,subQ10,subQ11])],"isStart":true})});}
            var sketch = newSketch(context, id + "F16", { "sketchPlane" : qUnion([Q0])});
            skCircle(sketch, "E79.0", {"center": v(60, 53.33) * mm, "radius": 4 * mm});
            skArc(sketch, "E79.1", {"start": v(90, 70) * mm, "mid": v(87.07, 77.07) * mm, "end": v(80, 80) * mm});
            skLineSegment(sketch, "E79.2", {"start": v(-80, 80) * mm, "end": v(80, 80) * mm});
            skArc(sketch, "E79.3", {"start": v(-80, 80) * mm, "mid": v(-87.07, 77.07) * mm, "end": v(-90, 70) * mm});
            skLineSegment(sketch, "E79.4", {"start": v(-90, -70) * mm, "end": v(-90, 70) * mm});
            skCircle(sketch, "E79.5", {"center": v(-60, 53.33) * mm, "radius": 4 * mm});
            skLineSegment(sketch, "E79.6", {"start": v(-60, 37.3) * mm, "end": v(-60, -37.3) * mm});
            skArc(sketch, "E79.7", {"start": v(-52.38, 47.01) * mm, "mid": v(-57.87, 43.47) * mm, "end": v(-60, 37.3) * mm});
            skArc(sketch, "E79.8", {"start": v(52.38, 47.01) * mm, "mid": v(0, 53.33) * mm, "end": v(-52.38, 47.01) * mm});
            skArc(sketch, "E79.9", {"start": v(60, 37.3) * mm, "mid": v(57.87, 43.47) * mm, "end": v(52.38, 47.01) * mm});
            skLineSegment(sketch, "E79.10", {"start": v(60, 37.3) * mm, "end": v(60, -37.3) * mm});
            skArc(sketch, "E79.11", {"start": v(52.38, -47.01) * mm, "mid": v(57.87, -43.47) * mm, "end": v(60, -37.3) * mm});
            skArc(sketch, "E79.12", {"start": v(-52.38, -47.01) * mm, "mid": v(0, -53.33) * mm, "end": v(52.38, -47.01) * mm});
            skArc(sketch, "E79.13", {"start": v(-60, -37.3) * mm, "mid": v(-57.87, -43.47) * mm, "end": v(-52.38, -47.01) * mm});
            skCircle(sketch, "E79.14", {"center": v(-60, -53.33) * mm, "radius": 4 * mm});
            skCircle(sketch, "E79.15", {"center": v(60, -53.33) * mm, "radius": 4 * mm});
            skArc(sketch, "E79.16", {"start": v(-90, -70) * mm, "mid": v(-87.07, -77.07) * mm, "end": v(-80, -80) * mm});
            skLineSegment(sketch, "E79.17", {"start": v(-80, -80) * mm, "end": v(80, -80) * mm});
            skArc(sketch, "E79.18", {"start": v(80, -80) * mm, "mid": v(87.07, -77.07) * mm, "end": v(90, -70) * mm});
            skLineSegment(sketch, "E79.19", {"start": v(90, -70) * mm, "end": v(90, 70) * mm});
            skLineSegment(sketch, "E80", {"start": v(0, 80) * mm, "end": v(0, 104.25) * mm, "construction": true});
            skCircle(sketch, "E81", {"center": v(0, 104.25) * mm, "radius": 6 * mm});
            skLineSegment(sketch, "E82", {"start": v(-32.98, 80) * mm, "end": v(-14.98, 98) * mm});
            skLineSegment(sketch, "E83", {"start": v(-14.98, 98) * mm, "end": v(-14.98, 110) * mm});
            skLineSegment(sketch, "E84", {"start": v(33.02, 80) * mm, "end": v(15.02, 98) * mm});
            skLineSegment(sketch, "E85", {"start": v(15.02, 98) * mm, "end": v(15.02, 110) * mm});
            skArc(sketch, "E86", {"start": v(15.02, 110) * mm, "mid": v(0.02, 125) * mm, "end": v(-14.98, 110) * mm});
            skLineSegment(sketch, "E87", {"start": v(-90, 0) * mm, "end": v(90, 0) * mm, "construction": true});
            skLineSegment(sketch, "E88.MirrorCS", {"start": v(-32.98, -80) * mm, "end": v(-14.98, -98) * mm});
            skLineSegment(sketch, "E89.MirrorCS", {"start": v(-14.98, -98) * mm, "end": v(-14.98, -110) * mm});
            skArc(sketch, "E90.MirrorCS", {"start": v(15.02, -110) * mm, "mid": v(0.02, -125) * mm, "end": v(-14.98, -110) * mm});
            skLineSegment(sketch, "E91.MirrorCS", {"start": v(15.02, -98) * mm, "end": v(15.02, -110) * mm});
            skLineSegment(sketch, "E92.MirrorCS", {"start": v(33.02, -80) * mm, "end": v(15.02, -98) * mm});
            skLineSegment(sketch, "E93.MirrorCS", {"start": v(0, -80) * mm, "end": v(0, -104.25) * mm, "construction": true});
            skCircle(sketch, "E94.MirrorC", {"center": v(0, -104.25) * mm, "radius": 6 * mm});
            skSolve(sketch);
        }
        {
            var Q0;
            Q0 = qSketchRegion(id + "F16", true);
            extrude(context, id + "F17", {"entities" : qUnion([Q0]), "operationType" : NewBodyOperationType.ADD, "endBound" : BoundingType.SYMMETRIC, "depth" : 6 * mm});
        }
    });
